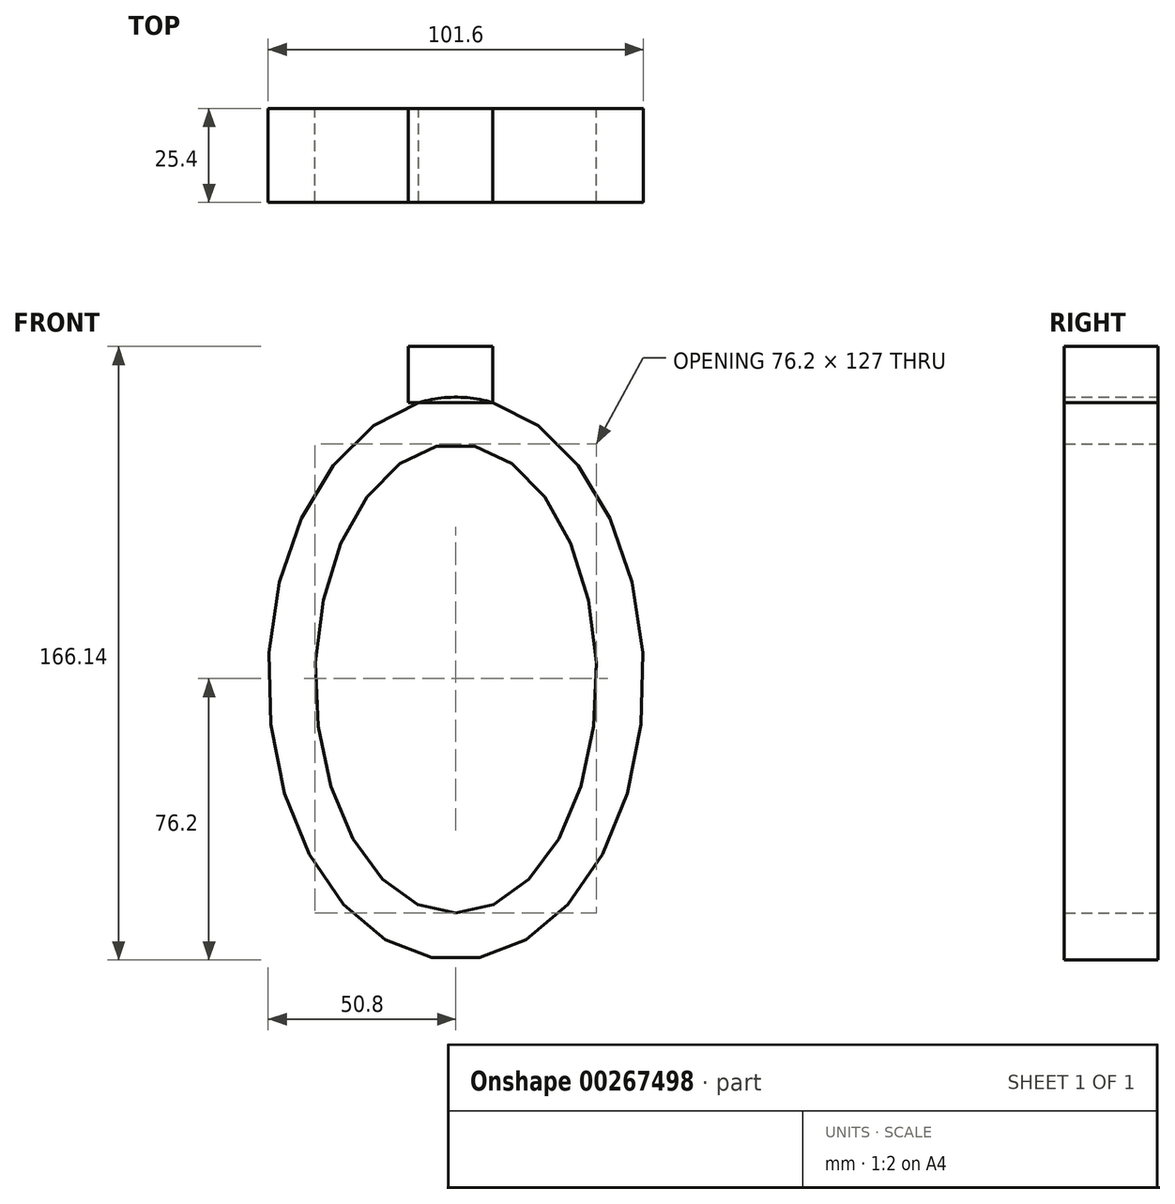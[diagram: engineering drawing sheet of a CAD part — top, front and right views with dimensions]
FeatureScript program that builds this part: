
annotation { "Feature Type Name" : "Feature", "Feature Type Description" : "" }
export const myFeature = defineFeature(function(context is Context, id is Id, definition is map)
    precondition{}
    {
        {
            var Q0;
            Q0=qCreatedBy(makeId("Front.planeOp"),FACE);
            var sketch = newSketch(context, id + "F0", { "sketchPlane" : qUnion([Q0])});
            skEllipse(sketch, "E0", {"center": v(0, 0) * mm, "majorRadius": 76.2 * mm, "minorRadius": 50.8 * mm, "majorAxis": v(0, -1)});
            skEllipse(sketch, "E1", {"center": v(0, 0) * mm, "majorRadius": 63.5 * mm, "minorRadius": 38.1 * mm, "majorAxis": v(0, -1)});
            skLineSegment(sketch, "E2.bottom", {"start": v(-12.84, 89.94) * mm, "end": v(10.02, 89.94) * mm});
            skLineSegment(sketch, "E2.top", {"start": v(-12.84, 74.7) * mm, "end": v(10.02, 74.7) * mm});
            skLineSegment(sketch, "E2.left", {"start": v(-12.84, 89.94) * mm, "end": v(-12.84, 74.7) * mm});
            skLineSegment(sketch, "E2.right", {"start": v(10.02, 89.94) * mm, "end": v(10.02, 74.7) * mm});
            skSolve(sketch);
        }
        {
            var Q0;
            Q0=makeQuery(id+"F0.imprint","IMPRINT",FACE,{"disambiguationData":[TD([[makeQuery(id+"F0.imprint","IMPRINT",EDGE,{"derivedFrom":sQuery(id+"F0.wireOp",EDGE,"E1")}),1.0]])]});
            var Q1;
            Q1=makeQuery(id+"F0.imprint","IMPRINT",FACE,{"disambiguationData":[TD([[makeQuery(id+"F0.imprint","IMPRINT",EDGE,{"derivedFrom":sQuery(id+"F0.wireOp",EDGE,"E0")}),1.0]])]});
            extrude(context, id + "F1", {"entities" : qUnion([Q0, Q1]), "depth" : 25.4 * mm});
        }
        {
            var Q0;
            Q0=makeQuery(id+"F0.imprint","IMPRINT",FACE,{"disambiguationData":[TD([[makeQuery(id+"F0.imprint","IMPRINT",EDGE,{"derivedFrom":sQuery(id+"F0.wireOp",EDGE,"E2.bottom")}),-1.0]])]});
            var Q1;
            {var subQ0=sQuery(id+"F0.wireOp",EDGE,"E2.top");var subQ1=sQuery(id+"F0.wireOp",EDGE,"E0");var subQ3=makeQuery(id+"F0.imprint","INTERSECT",VERTEX,{"derivedFrom":[subQ1,subQ0]});Q1=makeQuery(id+"F0.imprint","IMPRINT",FACE,{"disambiguationData":[TD([[makeQuery(id+"F0.imprint","IMPRINT",EDGE,{"disambiguationData":[TD([[subQ3,1.0]])],"derivedFrom":subQ1}),1.0]])]});}
            extrude(context, id + "F2", {"entities" : qUnion([Q0, Q1]), "depth" : 25.4 * mm});
        }
        {
            var Q0;
            Q0 = qSketchRegion(id + "F0", true);
            extrude(context, id + "F3", {"entities" : qUnion([Q0]), "depth" : 25.4 * mm});
        }
    });
